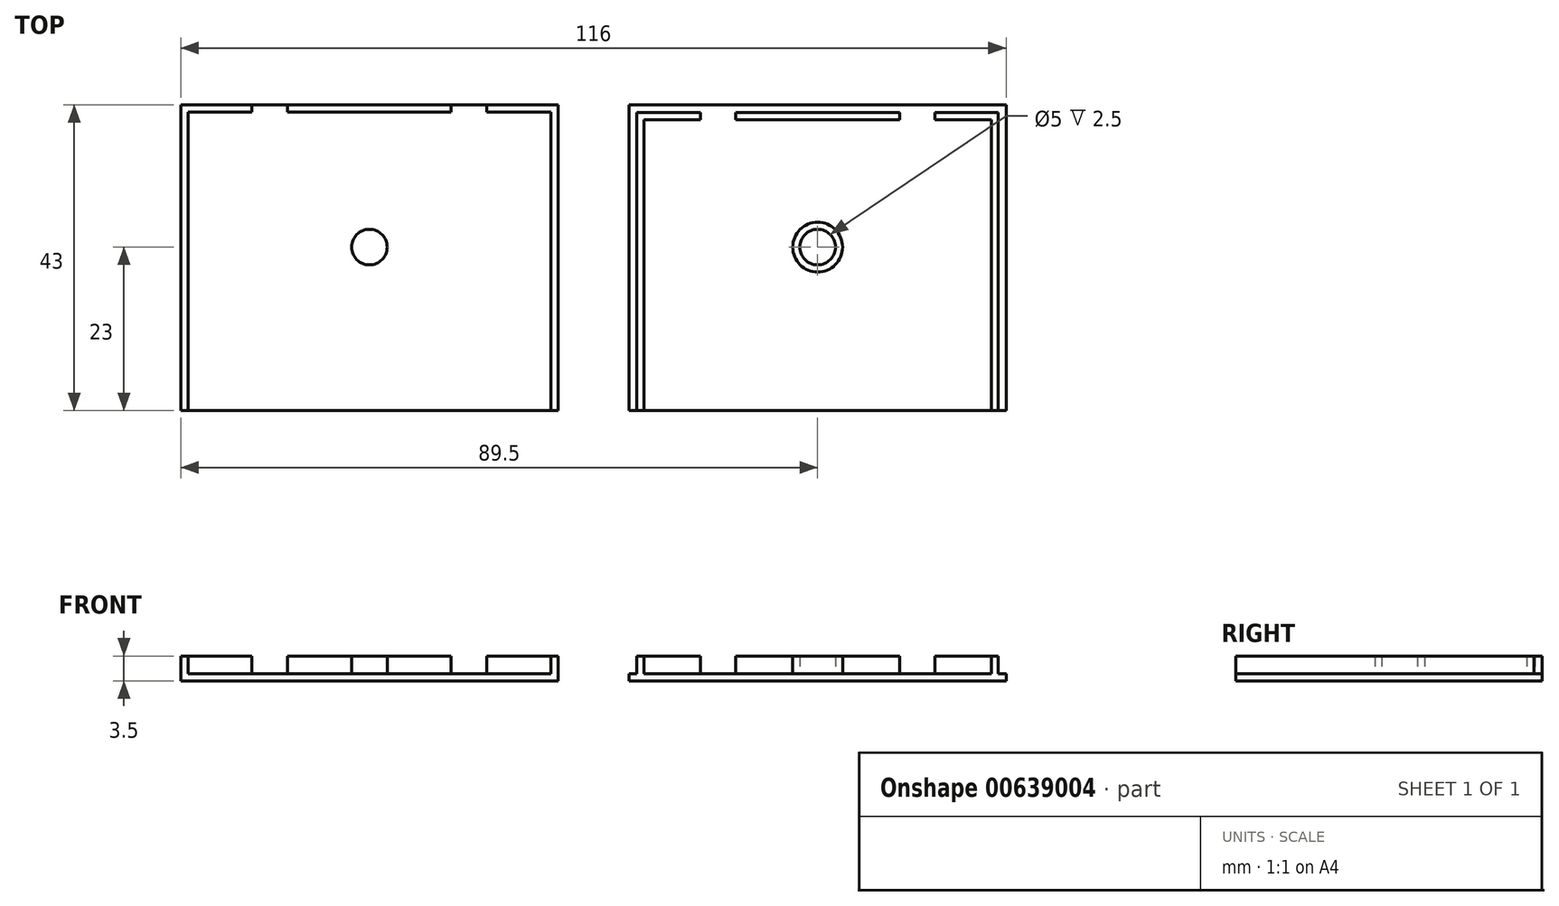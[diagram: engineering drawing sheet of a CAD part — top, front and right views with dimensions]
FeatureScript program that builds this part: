
annotation { "Feature Type Name" : "Feature", "Feature Type Description" : "" }
export const myFeature = defineFeature(function(context is Context, id is Id, definition is map)
    precondition{}
    {
        {
            var Q0;
            Q0=qCreatedBy(makeId("Top.planeOp"),FACE);
            var sketch = newSketch(context, id + "F0", { "sketchPlane" : qUnion([Q0])});
            skLineSegment(sketch, "E0.bottom", {"start": v(-58, -23) * mm, "end": v(-5, -23) * mm});
            skLineSegment(sketch, "E0.top", {"start": v(-58, 20) * mm, "end": v(-5, 20) * mm});
            skLineSegment(sketch, "E0.left", {"start": v(-58, -23) * mm, "end": v(-58, 20) * mm});
            skLineSegment(sketch, "E0.right", {"start": v(-5, -23) * mm, "end": v(-5, 20) * mm});
            skCircle(sketch, "E1", {"center": v(-31.5, 0) * mm, "radius": 2.5 * mm});
            skLineSegment(sketch, "E2", {"start": v(-40, 20) * mm, "end": v(-40, -3) * mm, "construction": true});
            skLineSegment(sketch, "E3", {"start": v(-23, 20) * mm, "end": v(-23, -3) * mm, "construction": true});
            skArc(sketch, "E4", {"start": v(-40, -3) * mm, "mid": v(-31.5, -8.2) * mm, "end": v(-23, -3) * mm, "construction": true});
            skLineSegment(sketch, "E5.0", {"start": v(-6, -35.8) * mm, "end": v(-6, 19) * mm});
            skLineSegment(sketch, "E5.1", {"start": v(-57, 19) * mm, "end": v(-6, 19) * mm});
            skLineSegment(sketch, "E5.2", {"start": v(-57, -35.8) * mm, "end": v(-57, 19) * mm});
            skLineSegment(sketch, "E6", {"start": v(-48, 19) * mm, "end": v(-48, 20) * mm});
            skLineSegment(sketch, "E7", {"start": v(-43, 19) * mm, "end": v(-43, 20) * mm});
            skLineSegment(sketch, "E8", {"start": v(-15, 20) * mm, "end": v(-15, 19) * mm});
            skLineSegment(sketch, "E9", {"start": v(-20, 20) * mm, "end": v(-20, 19) * mm});
            skSolve(sketch);
        }
        {
            var Q0;
            Q0=makeQuery(id+"F0.imprint","IMPRINT",FACE,{"disambiguationData":[TD([[makeQuery(id+"F0.imprint","IMPRINT",EDGE,{"derivedFrom":sQuery(id+"F0.wireOp",EDGE,"E1")}),-1.0]])]});
            var Q1;
            {var subQ0=sQuery(id+"F0.wireOp",EDGE,"E8");Q1=makeQuery(id+"F0.imprint","IMPRINT",FACE,{"disambiguationData":[TD([[makeQuery(id+"F0.imprint","IMPRINT",EDGE,{"derivedFrom":subQ0}),-1.0]])]});}
            var Q2;
            {var subQ0=sQuery(id+"F0.wireOp",EDGE,"E6");Q2=makeQuery(id+"F0.imprint","IMPRINT",FACE,{"disambiguationData":[TD([[makeQuery(id+"F0.imprint","IMPRINT",EDGE,{"derivedFrom":subQ0}),-1.0]])]});}
            extrude(context, id + "F1", {"entities" : qUnion([Q0, Q1, Q2]), "depth" : 1 * mm, "offsetDistance" : 25 * mm});
        }
        {
            var Q0;
            {var subQ3=sQuery(id+"F0.wireOp",EDGE,"E0.left");Q0=makeQuery(id+"F0.imprint","IMPRINT",FACE,{"disambiguationData":[TD([[makeQuery(id+"F0.imprint","IMPRINT",EDGE,{"derivedFrom":subQ3}),-1.0]])]});}
            var Q1;
            {var subQ0=sQuery(id+"F0.wireOp",EDGE,"E7");Q1=makeQuery(id+"F0.imprint","IMPRINT",FACE,{"disambiguationData":[TD([[makeQuery(id+"F0.imprint","IMPRINT",EDGE,{"derivedFrom":subQ0}),-1.0]])]});}
            var Q2;
            {var subQ1=sQuery(id+"F0.wireOp",EDGE,"E0.right");Q2=makeQuery(id+"F0.imprint","IMPRINT",FACE,{"disambiguationData":[TD([[makeQuery(id+"F0.imprint","IMPRINT",EDGE,{"derivedFrom":subQ1}),1.0]])]});}
            extrude(context, id + "F2", {"entities" : qUnion([Q0, Q1, Q2]), "operationType" : NewBodyOperationType.ADD, "depth" : 3.5 * mm, "offsetDistance" : 25 * mm});
        }
        {
            var Q0;
            Q0=makeQuery(id+"F0.imprint","IMPRINT",FACE,{"disambiguationData":[TD([[makeQuery(id+"F0.imprint","IMPRINT",EDGE,{"derivedFrom":sQuery(id+"F0.wireOp",EDGE,"E1")}),1.0]])]});
            extrude(context, id + "F3", {"entities" : qUnion([Q0]), "operationType" : NewBodyOperationType.ADD, "depth" : 3.5 * mm, "offsetDistance" : 25 * mm});
        }
        {
            var Q0;
            Q0=qCreatedBy(makeId("Top.planeOp"),FACE);
            var sketch = newSketch(context, id + "F4", { "sketchPlane" : qUnion([Q0])});
            skLineSegment(sketch, "E10.bottom", {"start": v(5, -23) * mm, "end": v(58, -23) * mm});
            skLineSegment(sketch, "E10.top", {"start": v(5, 20) * mm, "end": v(58, 20) * mm});
            skLineSegment(sketch, "E10.left", {"start": v(5, -23) * mm, "end": v(5, 20) * mm});
            skLineSegment(sketch, "E10.right", {"start": v(58, -23) * mm, "end": v(58, 20) * mm});
            skCircle(sketch, "E11", {"center": v(31.5, 0) * mm, "radius": 2.5 * mm});
            skLineSegment(sketch, "E12", {"start": v(23, 20) * mm, "end": v(23, -3) * mm, "construction": true});
            skLineSegment(sketch, "E13", {"start": v(40, 20) * mm, "end": v(40, -3) * mm, "construction": true});
            skArc(sketch, "E14", {"start": v(23, -3) * mm, "mid": v(31.5, -8.2) * mm, "end": v(40, -3) * mm, "construction": true});
            skLineSegment(sketch, "E15.0", {"start": v(56.9, -37.72) * mm, "end": v(56.9, 18.9) * mm});
            skLineSegment(sketch, "E15.1", {"start": v(6.1, 18.9) * mm, "end": v(56.9, 18.9) * mm});
            skLineSegment(sketch, "E15.2", {"start": v(6.1, -37.72) * mm, "end": v(6.1, 18.9) * mm});
            skLineSegment(sketch, "E16", {"start": v(15, 18.9) * mm, "end": v(15, 20) * mm});
            skLineSegment(sketch, "E17", {"start": v(20, 18.9) * mm, "end": v(20, 20) * mm});
            skLineSegment(sketch, "E18", {"start": v(48, 20) * mm, "end": v(48, 18.9) * mm});
            skLineSegment(sketch, "E19", {"start": v(43, 20) * mm, "end": v(43, 18.9) * mm});
            skLineSegment(sketch, "E20.0", {"start": v(55.9, -37.72) * mm, "end": v(55.9, 17.9) * mm});
            skLineSegment(sketch, "E20.1", {"start": v(7.1, 17.9) * mm, "end": v(55.9, 17.9) * mm});
            skLineSegment(sketch, "E20.2", {"start": v(7.1, -37.72) * mm, "end": v(7.1, 17.9) * mm});
            skCircle(sketch, "E21.0", {"center": v(31.5, 0) * mm, "radius": 3.5 * mm});
            skLineSegment(sketch, "E22", {"start": v(15, 18.9) * mm, "end": v(15, 17.9) * mm});
            skLineSegment(sketch, "E23", {"start": v(20, 18.9) * mm, "end": v(20, 17.9) * mm});
            skLineSegment(sketch, "E24", {"start": v(43, 18.9) * mm, "end": v(43, 17.9) * mm});
            skLineSegment(sketch, "E25", {"start": v(48, 18.9) * mm, "end": v(48, 17.9) * mm});
            skSolve(sketch);
        }
        {
            var Q0;
            {var subQ3=sQuery(id+"F4.wireOp",EDGE,"E10.left");Q0=makeQuery(id+"F4.imprint","IMPRINT",FACE,{"disambiguationData":[TD([[makeQuery(id+"F4.imprint","IMPRINT",EDGE,{"derivedFrom":subQ3}),-1.0]])]});}
            var Q1;
            {var subQ0=sQuery(id+"F4.wireOp",EDGE,"E17");Q1=makeQuery(id+"F4.imprint","IMPRINT",FACE,{"disambiguationData":[TD([[makeQuery(id+"F4.imprint","IMPRINT",EDGE,{"derivedFrom":subQ0}),-1.0]])]});}
            var Q2;
            {var subQ1=sQuery(id+"F4.wireOp",EDGE,"E10.right");Q2=makeQuery(id+"F4.imprint","IMPRINT",FACE,{"disambiguationData":[TD([[makeQuery(id+"F4.imprint","IMPRINT",EDGE,{"derivedFrom":subQ1}),1.0]])]});}
            var Q3;
            {var subQ1=sQuery(id+"F4.wireOp",EDGE,"E20.0");Q3=makeQuery(id+"F4.imprint","IMPRINT",FACE,{"disambiguationData":[TD([[makeQuery(id+"F4.imprint","IMPRINT",EDGE,{"derivedFrom":subQ1}),1.0]])]});}
            var Q4;
            {var subQ0=sQuery(id+"F4.wireOp",EDGE,"E16");Q4=makeQuery(id+"F4.imprint","IMPRINT",FACE,{"disambiguationData":[TD([[makeQuery(id+"F4.imprint","IMPRINT",EDGE,{"derivedFrom":subQ0}),-1.0]])]});}
            var Q5;
            {var subQ0=sQuery(id+"F4.wireOp",EDGE,"E18");Q5=makeQuery(id+"F4.imprint","IMPRINT",FACE,{"disambiguationData":[TD([[makeQuery(id+"F4.imprint","IMPRINT",EDGE,{"derivedFrom":subQ0}),-1.0]])]});}
            var Q6;
            Q6=makeQuery(id+"F4.imprint","IMPRINT",FACE,{"disambiguationData":[TD([[makeQuery(id+"F4.imprint","IMPRINT",EDGE,{"derivedFrom":sQuery(id+"F4.wireOp",EDGE,"E11")}),1.0]])]});
            var Q7;
            {var subQ0=sQuery(id+"F4.wireOp",EDGE,"E22");Q7=makeQuery(id+"F4.imprint","IMPRINT",FACE,{"disambiguationData":[TD([[makeQuery(id+"F4.imprint","IMPRINT",EDGE,{"derivedFrom":subQ0}),1.0]])]});}
            var Q8;
            {var subQ2=sQuery(id+"F4.wireOp",EDGE,"E24");Q8=makeQuery(id+"F4.imprint","IMPRINT",FACE,{"disambiguationData":[TD([[makeQuery(id+"F4.imprint","IMPRINT",EDGE,{"derivedFrom":subQ2}),1.0]])]});}
            var Q9;
            Q9=makeQuery(id+"F4.imprint","IMPRINT",FACE,{"disambiguationData":[TD([[makeQuery(id+"F4.imprint","IMPRINT",EDGE,{"derivedFrom":sQuery(id+"F4.wireOp",EDGE,"E11")}),-1.0]])]});
            extrude(context, id + "F5", {"entities" : qUnion([Q0, Q1, Q2, Q3, Q4, Q5, Q6, Q7, Q8, Q9]), "depth" : 1 * mm, "offsetDistance" : 25 * mm});
        }
        {
            var Q0;
            {var subQ3=sQuery(id+"F4.wireOp",EDGE,"E15.2");Q0=makeQuery(id+"F4.imprint","IMPRINT",FACE,{"disambiguationData":[TD([[makeQuery(id+"F4.imprint","IMPRINT",EDGE,{"derivedFrom":subQ3}),-1.0]])]});}
            var Q1;
            {var subQ0=sQuery(id+"F4.wireOp",EDGE,"E23");Q1=makeQuery(id+"F4.imprint","IMPRINT",FACE,{"disambiguationData":[TD([[makeQuery(id+"F4.imprint","IMPRINT",EDGE,{"derivedFrom":subQ0}),1.0]])]});}
            var Q2;
            {var subQ1=sQuery(id+"F4.wireOp",EDGE,"E15.0");Q2=makeQuery(id+"F4.imprint","IMPRINT",FACE,{"disambiguationData":[TD([[makeQuery(id+"F4.imprint","IMPRINT",EDGE,{"derivedFrom":subQ1}),1.0]])]});}
            extrude(context, id + "F6", {"entities" : qUnion([Q0, Q1, Q2]), "operationType" : NewBodyOperationType.ADD, "depth" : 3.5 * mm, "offsetDistance" : 25 * mm});
        }
        {
            var Q0;
            Q0=makeQuery(id+"F4.imprint","IMPRINT",FACE,{"disambiguationData":[TD([[makeQuery(id+"F4.imprint","IMPRINT",EDGE,{"derivedFrom":sQuery(id+"F4.wireOp",EDGE,"E11")}),-1.0]])]});
            extrude(context, id + "F7", {"entities" : qUnion([Q0]), "operationType" : NewBodyOperationType.ADD, "depth" : 3.5 * mm, "offsetDistance" : 25 * mm});
        }
    });
